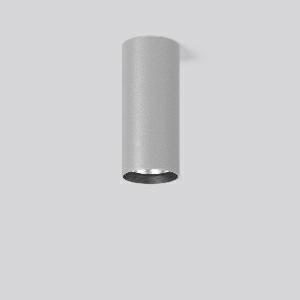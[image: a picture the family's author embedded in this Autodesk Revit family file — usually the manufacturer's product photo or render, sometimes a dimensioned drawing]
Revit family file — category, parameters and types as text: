
# Revit family: heledon_mini_a_931208_004_3_76_fdaa
name_source: partatom
category: Lighting Fixtures
units: mm (PartAtom-declared; Revit-internal decimal feet)

## family parameters
Cut with Voids When Loaded = No
Host = Face
Light Source = No
Part Type = Normal
Room Calculation Point = No
Round Connector Dimension = Use Diameter
Shared = No

## types (1)
- HELEDON mini A (1 x LED Modul 935, 3700 lm, 3500)
    Apparent Load = 29 VA
    Approval mark = CE
    CIE Flux Codes = 100 100 100 100 100
    Color Rendering = 92
    Color Temperature = 3500
    Default Elevation = 1800 mm
    Description = Series: HELEDON mini
Cylindrical surface-mounted downlight. Housing: die-cast aluminium, powder-coated. Internal ceiling frame polycarbonate with bayonet mounting. Black plastic ring and recessed LED to prevent glare from the side. Optical assembly with reflector made of MIRO-Silver with 98% total light reflection for outstanding efficiency - can be changed without tools. Best colour rendering index Ra>90. Suitable for Ceiling mounting. Easy installation with a separate ceiling frame with bayonet mounting and plug connection. Driver integrated. Connected via plug-in connector. High quality converter without flickering and stroboscopic effect. The following accessories can be mounted without use of tools: interchangeable lenses, decorative glasses, honeycomb louvre, clear and frosted diffusers, white interchangeable plastic ring. 
Colour: silver
Diameter: 87 mm
Height: 197 mm
Lamp: LED
Socket: without socket
Colour temperature: 3500K
Colour rendering index (CRI): 92
System power: 29 W
Rated luminous flux: 3700 lm
Luminous efficiency: 128 lm/W
Control gear: Converter, dimmable, DALI
Protection class: I
Type of protection: IP 20
    Height = 197 mm
    Lamp = 1 x LED Modul 935
    Lamp Light Flux = 3700 lm
    Lamp count = 1
    Length = 87 mm
    Lifetime = 50000 h
    Luminous efficacy = 128 lm/W
    Manufacturer = RZB
    ModVariant = No
    Model = 931208.004.3.76
    Mounting Place = Ceiling
    Mounting Type = Surface mounted
    Number of Poles = 1
    OnlyDefault = Yes
    Power Factor = 1
    Product Name = HELEDON mini A
    Product group = Surface mounted downlights
    ProductGroupID = 302
    Protection Class = Protection class I
    Protection Degree = IP 20
    RLX_Detail_Level = 1
    RLX_Emergency_Light_Flux = 0 lm
    RLX_Emergency_Type = 0
    RLX_Emergency_Type_DB = No
    RlxData = <blob elided: 107281 chars, md5=4cd037fe>
    Socket = socket
    Standby Power = 0 W
    System Light Flux = 3700 lm
    System Power = 29 W
    Type Comments = Product without accessories
    Type Image = 931188.004.jpg
    URL = http://relux.com
    VarID = ---
    Voltage = 230 V
    Voltage Range = 220-240 V
    Weight = 0.00 kg
    Width = 0 mm  [stored 0 ft]

note: [stored X ft] marks values corroborated as IEEE doubles in the binary element streams (Revit-internal decimal feet)

## geometry (parser evidence)
native form markers: Blend x4, Sweep x8
no freeform markers — native parametric forms only
